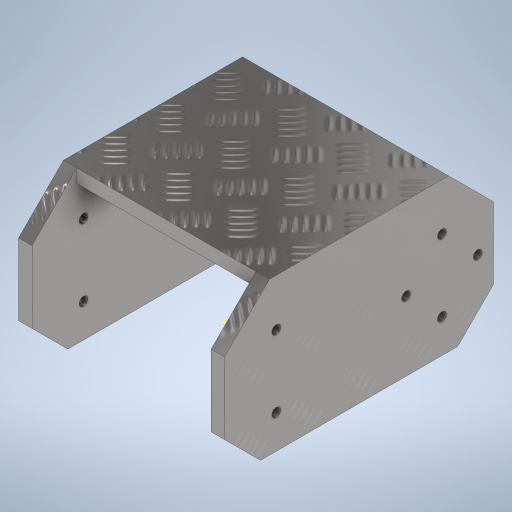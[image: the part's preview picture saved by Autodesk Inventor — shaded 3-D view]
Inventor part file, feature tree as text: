
AUTODESK INVENTOR PART (.ipt)
format: ipt  version: 2024 (Build 280153000, 153)  size: 355,328 bytes
history: native  units: in
note: dims shown in document units (in); Inventor stores cm internally (conversion verified against a paired STEP export)
features: sketch x9, extrude x8
ambient origin geometry x8: Origin, YZ Plane, XZ Plane, XY Plane, X Axis, Y Axis, Z Axis, Center Point
bodies: Solid1 (feature_tree)
feature tree (17):
  extrude  "Extrusion1"  Depth=2.3622in
  extrude  "Extrusion2"  Depth=0.1181in
  extrude  "Extrusion3"  Depth=2.3622in
  sketch  "Sketch4"  dims[d7=1.2205in d8=0.0in d16=0.4528in]
  extrude  "Extrusion4"  Depth=1.2205in
  extrude  "Extrusion5"  Depth=0.315in
  extrude  "Extrusion7"  Depth=0.1181in TaperAngle=0.0deg
  extrude  "Extrusion8"  Depth=0.315in
  extrude  "Extrusion9"  Depth=0.315in
  sketch  "Sketch1"  dims[d0=1.811in d1=2.3622in]
  sketch  "Sketch2"  dims[d2=0.1181in d3=0.0in d4=0.1181in]
  sketch  "Sketch3"  dims[d5=0.1181in d6=2.3622in]
  sketch  "Sketch5"  dims[d17=0.0787in d18=0.315in]
  sketch  "Sketch6"  dims[d19=1.5748in d21=360.0deg d23=0.1181in d24=0.0in]
  sketch  "Sketch8"  dims[d25=0.315in d26=0.315in]
  sketch  "Sketch9"  dims[d27=0.315in d28=0.315in]
  sketch  "Sketch10"  dims[d29=1.9685in d30=0.0in d31=0.3937in d32=1.5748in d33=0.3937in d34=0.3937in d35=0.0in d38=0.6102in d39=90.0deg d40=0.6102in d41=0.1181in d42=0.4528in d43=0.1181in d44=0.0in d47=0.4528in d49=0.6102in d50=0.0787in d51=0.315in d52=1.9685in d53=0.0in d54=0.3937in d55=0.3937in d56=0.3937in d57=0.3937in d58=1.9685in d59=0.0in]
